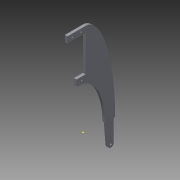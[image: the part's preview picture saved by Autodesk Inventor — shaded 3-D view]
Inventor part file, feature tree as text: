
AUTODESK INVENTOR PART (.ipt)
format: ipt  version: 2015 (Build 190159000, 159)  size: 114,688 bytes
history: native  units: mm
features: sketch x2, extrude x1, fillet x1
ambient origin geometry x8: Origin, YZ Plane, XZ Plane, XY Plane, X Axis, Y Axis, Z Axis, Center Point
bodies: Body1 (feature_tree)
feature tree (4):
  sketch  "Sketch1"  dims[d0=106.0mm d5=33.5mm d6=106.0mm]
  sketch  "Sketch2"  dims[d10=20.5mm d12=28.5mm d14=6.5mm d15=7.0mm d16=40.5mm d17=1.5mm d18=1.5mm d22=3.5mm d23=5.0mm d24=1.5mm d25=1.5mm d26=5.5mm d29=1.5mm d32=25.0mm d34=24.5mm d35=6.5mm d36=2.0mm d39=10.25mm d40=3.0mm d41=0.0mm d42=2.0mm]
  extrude  "Extrusion2"  Depth=106.0mm
  fillet  "Fillet1"  Radius=106.0mm
